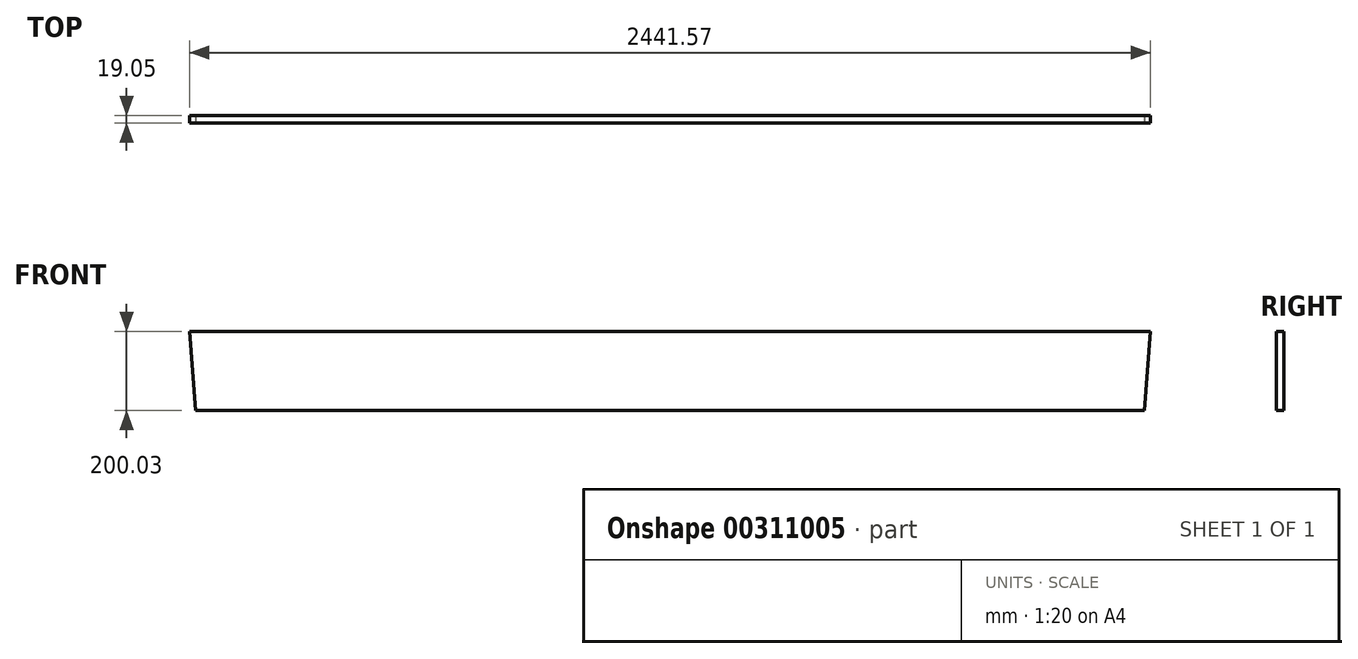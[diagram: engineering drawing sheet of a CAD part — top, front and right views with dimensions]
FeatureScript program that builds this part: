
annotation { "Feature Type Name" : "Feature", "Feature Type Description" : "" }
export const myFeature = defineFeature(function(context is Context, id is Id, definition is map)
    precondition{}
    {
        {
            var Q0;
            Q0=qCreatedBy(makeId("Front.planeOp"),FACE);
            var sketch = newSketch(context, id + "F0", { "sketchPlane" : qUnion([Q0])});
            skLineSegment(sketch, "E0", {"start": v(0, 0) * mm, "end": v(2441.58, 0) * mm});
            skLineSegment(sketch, "E1", {"start": v(2441.58, 0) * mm, "end": v(2425.7, -200.03) * mm});
            skLineSegment(sketch, "E2", {"start": v(2425.7, -200.03) * mm, "end": v(15.88, -200.03) * mm});
            skLineSegment(sketch, "E3", {"start": v(15.88, -200.03) * mm, "end": v(0, 0) * mm});
            skSolve(sketch);
        }
        {
            var Q0;
            Q0=makeQuery(id+"F0.imprint","IMPRINT",FACE,{"disambiguationData":[TD([[makeQuery(id+"F0.imprint","IMPRINT",EDGE,{"derivedFrom":sQuery(id+"F0.wireOp",EDGE,"E0")}),-1.0]])]});
            extrude(context, id + "F1", {"entities" : qUnion([Q0]), "oppositeDirection" : true, "depth" : 19.05 * mm});
        }
    });
